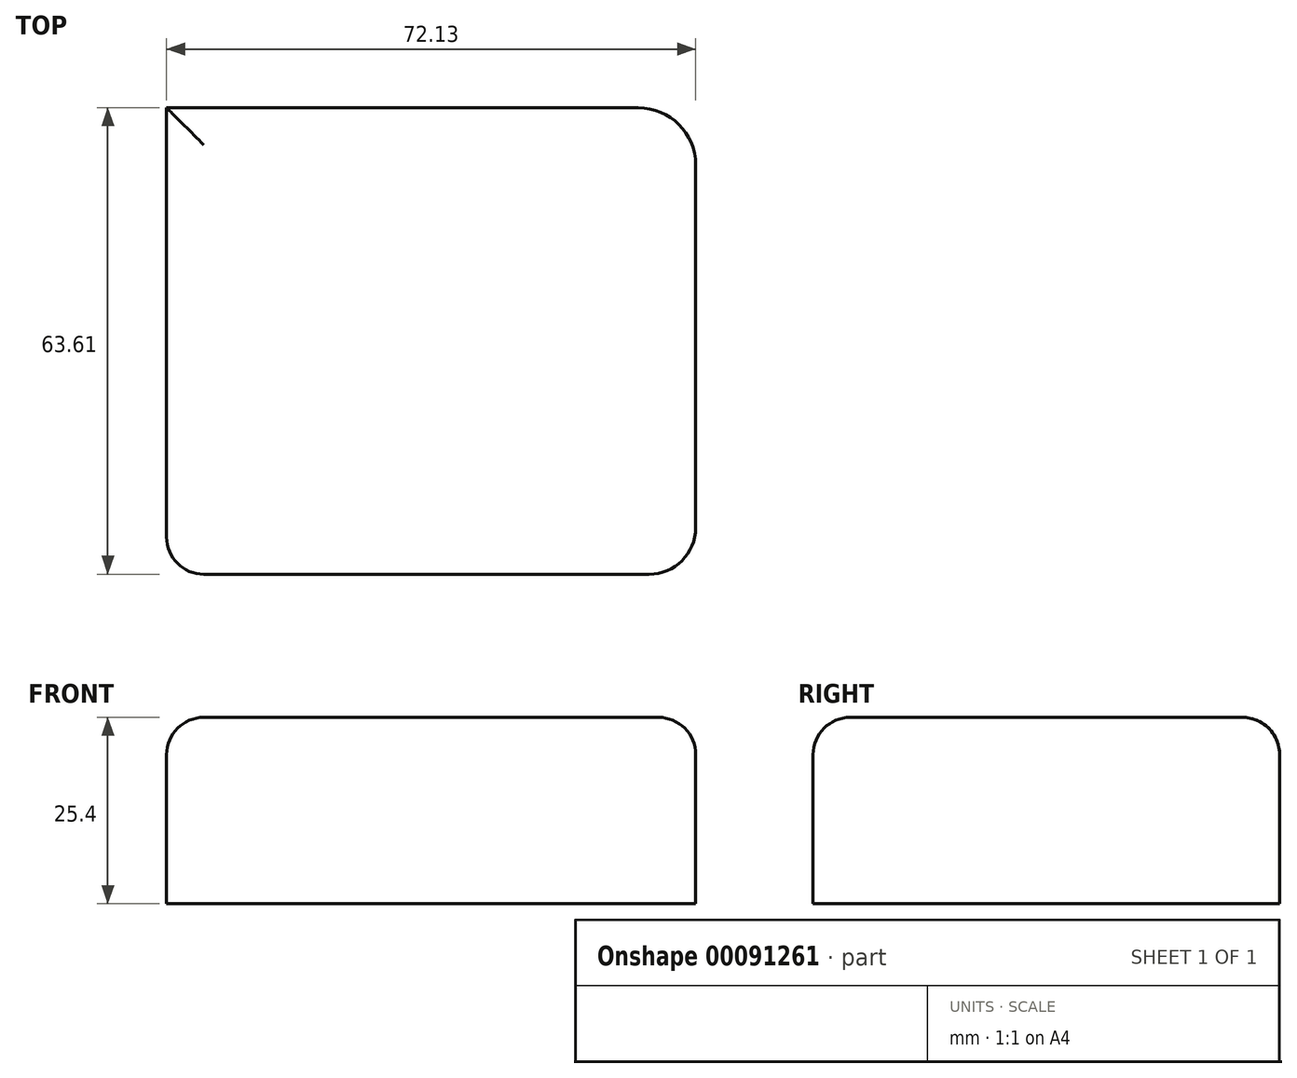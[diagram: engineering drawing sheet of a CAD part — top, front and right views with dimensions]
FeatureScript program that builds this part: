
annotation { "Feature Type Name" : "Feature", "Feature Type Description" : "" }
export const myFeature = defineFeature(function(context is Context, id is Id, definition is map)
    precondition{}
    {
        {
            var Q0;
            Q0=qCreatedBy(makeId("Top.planeOp"),FACE);
            var sketch = newSketch(context, id + "F0", { "sketchPlane" : qUnion([Q0])});
            skLineSegment(sketch, "E0.bottom", {"start": v(0, 0) * mm, "end": v(65.78, 0) * mm});
            skLineSegment(sketch, "E0.top", {"start": v(0, 63.61) * mm, "end": v(64.32, 63.61) * mm});
            skLineSegment(sketch, "E0.left", {"start": v(0, 0) * mm, "end": v(0, 63.61) * mm});
            skLineSegment(sketch, "E0.right", {"start": v(72.13, 6.35) * mm, "end": v(72.13, 55.8) * mm});
            skArc(sketch, "E1", {"start": v(72.13, 55.8) * mm, "mid": v(69.84, 61.32) * mm, "end": v(64.32, 63.61) * mm});
            skPoint(sketch, "E2.visualSharp", {"position": v(72.13, 0) * mm});
            skArc(sketch, "E2.filletArc", {"start": v(65.78, 0) * mm, "mid": v(70.27, 1.86) * mm, "end": v(72.13, 6.35) * mm});
            skSolve(sketch);
        }
        {
            var Q0;
            Q0 = qSketchRegion(id + "F0", true);
            extrude(context, id + "F1", {"entities" : qUnion([Q0]), "depth" : 25.4 * mm});
        }
        {
            var Q0;
            Q0=makeQuery(id+"F1.opExtrude","CAP_EDGE",EDGE,{"disambiguationData":[OSD([sQuery(id+"F0.wireOp",EDGE,"E0.bottom")])],"isStart":false});
            var Q1;
            Q1=makeQuery(id+"F1.opExtrude","CAP_EDGE",EDGE,{"disambiguationData":[OSD([sQuery(id+"F0.wireOp",EDGE,"E0.left")])],"isStart":false});
            var Q2;
            Q2=makeQuery(id+"F1.opExtrude","SWEPT_EDGE",EDGE,{"disambiguationData":[OSD([sQuery(id+"F0.wireOp",EDGE,"E0.bottom"),sQuery(id+"F0.wireOp",EDGE,"E0.left")])]});
            fillet(context, id + "F2", {"entities" : qUnion([Q0, Q1, Q2]), "radius" : 5.08 * mm, "tangentPropagation" : true, "allowEdgeOverflow" : false});
        }
    });
